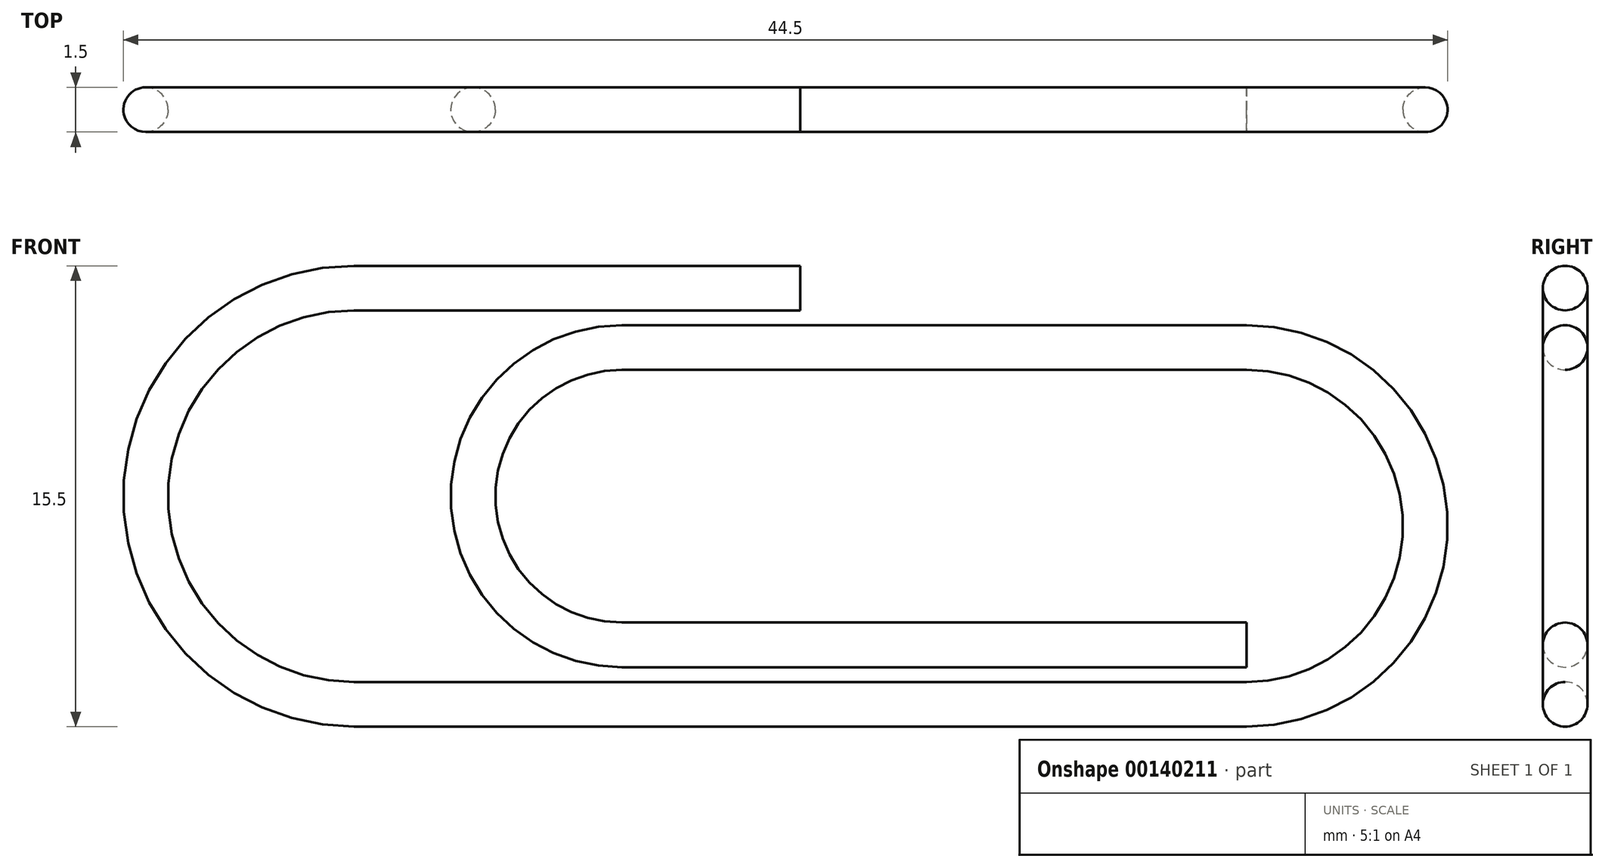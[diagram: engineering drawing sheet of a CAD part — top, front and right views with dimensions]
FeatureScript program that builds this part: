
annotation { "Feature Type Name" : "Feature", "Feature Type Description" : "" }
export const myFeature = defineFeature(function(context is Context, id is Id, definition is map)
    precondition{}
    {
        {
            var Q0;
            Q0=qCreatedBy(makeId("Front.planeOp"),FACE);
            var sketch = newSketch(context, id + "F0", { "sketchPlane" : qUnion([Q0])});
            skLineSegment(sketch, "E0", {"start": v(0, 0) * mm, "end": v(0, 17.02) * mm, "construction": true});
            skLineSegment(sketch, "E1", {"start": v(-15, 17.3) * mm, "end": v(-15, 0) * mm, "construction": true});
            skLineSegment(sketch, "E2", {"start": v(15, 0) * mm, "end": v(15, 17.62) * mm, "construction": true});
            skLineSegment(sketch, "E3", {"start": v(15, 1) * mm, "end": v(-15, 1) * mm});
            skArc(sketch, "E4", {"start": v(-15, 15) * mm, "mid": v(-22, 8) * mm, "end": v(-15, 1) * mm});
            skLineSegment(sketch, "E5", {"start": v(-15, 15) * mm, "end": v(0, 15) * mm});
            skArc(sketch, "E6", {"start": v(15, 1) * mm, "mid": v(21, 7) * mm, "end": v(15, 13) * mm});
            skLineSegment(sketch, "E7", {"start": v(15, 13) * mm, "end": v(-6, 13) * mm});
            skArc(sketch, "E8", {"start": v(-6, 13) * mm, "mid": v(-11, 8) * mm, "end": v(-6, 3) * mm});
            skLineSegment(sketch, "E9", {"start": v(-6, 3) * mm, "end": v(15, 3) * mm});
            skSolve(sketch);
        }
        {
            var Q0;
            Q0=qCreatedBy(makeId("Right.planeOp"),FACE);
            var sketch = newSketch(context, id + "F1", { "sketchPlane" : qUnion([Q0])});
            skCircle(sketch, "E10", {"center": v(0, 15) * mm, "radius": 0.75 * mm});
            skSolve(sketch);
        }
        {
            var Q0;
            Q0=makeQuery(id+"F1.imprint","IMPRINT",FACE,{"disambiguationData":[TD([[makeQuery(id+"F1.imprint","IMPRINT",EDGE,{"derivedFrom":sQuery(id+"F1.wireOp",EDGE,"E10")}),1.0]])]});
            var Q1;
            Q1=sQuery(id+"F0.wireOp",EDGE,"E5");
            var Q2;
            Q2=sQuery(id+"F0.wireOp",EDGE,"E4");
            var Q3;
            Q3=sQuery(id+"F0.wireOp",EDGE,"E3");
            var Q4;
            Q4=sQuery(id+"F0.wireOp",EDGE,"E6");
            var Q5;
            Q5=sQuery(id+"F0.wireOp",EDGE,"E7");
            var Q6;
            Q6=sQuery(id+"F0.wireOp",EDGE,"E8");
            var Q7;
            Q7=sQuery(id+"F0.wireOp",EDGE,"E9");
            sweep(context, id + "F2", {"profiles" : qUnion([Q0]), "path" : qUnion([Q1, Q2, Q3, Q4, Q5, Q6, Q7])});
        }
    });
